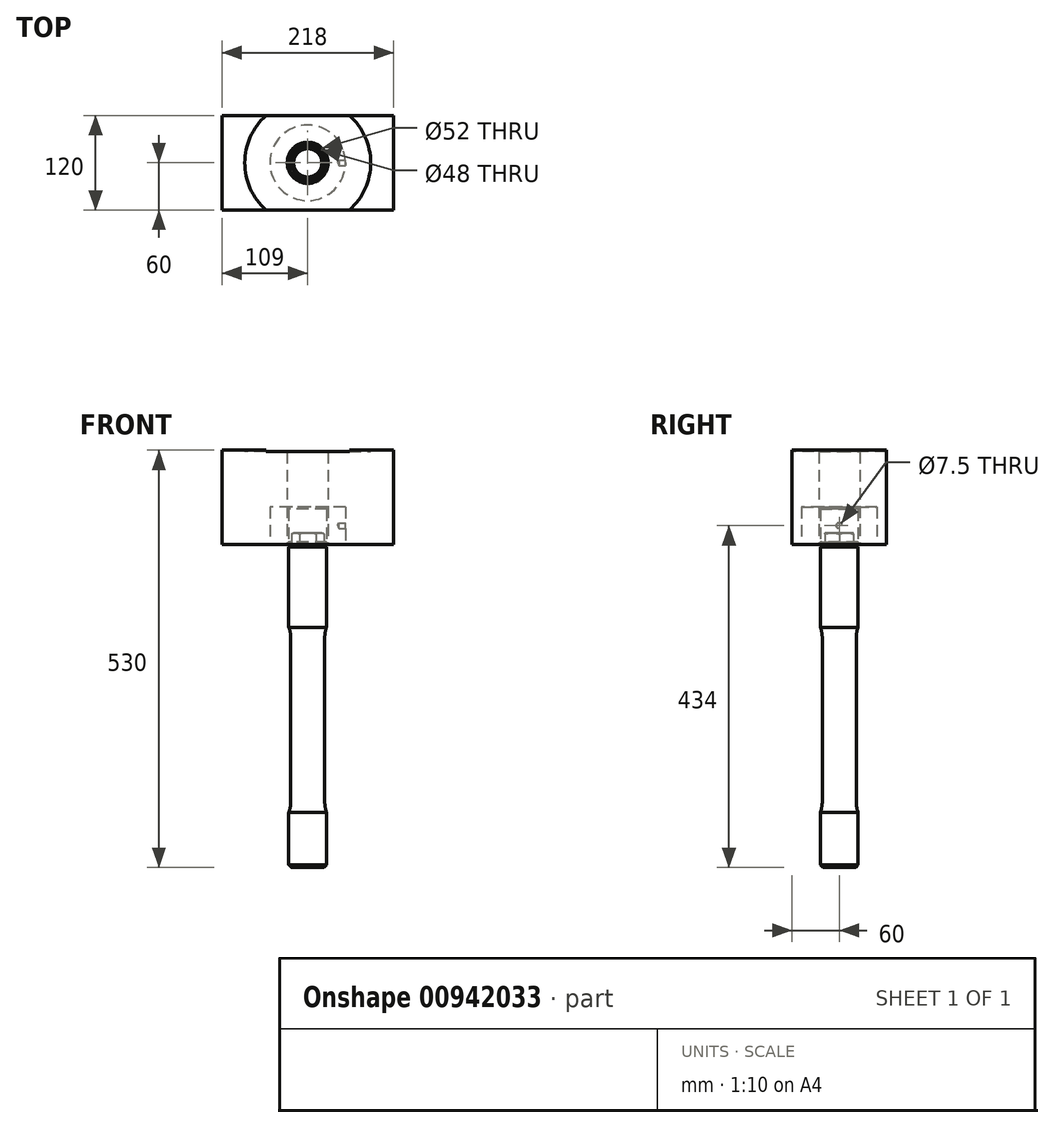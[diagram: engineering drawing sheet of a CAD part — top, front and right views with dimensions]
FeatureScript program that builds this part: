
annotation { "Feature Type Name" : "Feature", "Feature Type Description" : "" }
export const myFeature = defineFeature(function(context is Context, id is Id, definition is map)
    precondition{}
    {
        {
            var Q0;
            Q0=qCreatedBy(makeId("Front.planeOp"),FACE);
            var sketch = newSketch(context, id + "F0", { "sketchPlane" : qUnion([Q0])});
            skLineSegment(sketch, "E0", {"start": v(0, 0) * mm, "end": v(24, 0) * mm});
            skLineSegment(sketch, "E1", {"start": v(24, 0) * mm, "end": v(24, -105) * mm});
            skLineSegment(sketch, "E2", {"start": v(21.65, -117.6) * mm, "end": v(21.65, -327.4) * mm});
            skArc(sketch, "E3", {"start": v(24, -105) * mm, "mid": v(22.24, -111.2) * mm, "end": v(21.65, -117.6) * mm});
            skLineSegment(sketch, "E4", {"start": v(0, 0) * mm, "end": v(0, -410) * mm, "construction": true});
            skArc(sketch, "E5", {"start": v(21.65, -327.4) * mm, "mid": v(22.24, -333.8) * mm, "end": v(24, -340) * mm});
            skLineSegment(sketch, "E6", {"start": v(24, -340) * mm, "end": v(24, -410) * mm});
            skLineSegment(sketch, "E7", {"start": v(24, -410) * mm, "end": v(0, -410) * mm});
            skLineSegment(sketch, "E8", {"start": v(0, 0) * mm, "end": v(0, -410) * mm});
            skSolve(sketch);
        }
        {
            var Q0;
            Q0 = qSketchRegion(id + "F0", true);
            var Q1;
            Q1=sQuery(id+"F0.wireOp",EDGE,"E4");
            revolve(context, id + "F1", {"surfaceOperationType" : NewSurfaceOperationType.NEW, "entities" : qUnion([Q0]), "axis" : qUnion([Q1]), "revolveType" : RevolveType.FULL});
        }
        {
            var Q0;
            Q0=qCreatedBy(makeId("Top.planeOp"),FACE);
            var sketch = newSketch(context, id + "F2", { "sketchPlane" : qUnion([Q0])});
            skCircle(sketch, "E9.cCircle", {"center": v(0, 0) * mm, "radius": 18 * mm, "construction": true});
            skLineSegment(sketch, "E9.0", {"start": v(10.4, -18) * mm, "end": v(-10.4, -18) * mm});
            skLineSegment(sketch, "E9.1", {"start": v(-10.4, -18) * mm, "end": v(-20.78, 0) * mm});
            skLineSegment(sketch, "E9.2", {"start": v(-20.78, 0) * mm, "end": v(-10.4, 18) * mm});
            skLineSegment(sketch, "E9.3", {"start": v(-10.4, 18) * mm, "end": v(10.4, 18) * mm});
            skLineSegment(sketch, "E9.4", {"start": v(10.4, 18) * mm, "end": v(20.78, 0) * mm});
            skLineSegment(sketch, "E9.5", {"start": v(20.78, 0) * mm, "end": v(10.4, -18) * mm});
            skPoint(sketch, "E9.0.midPoint", {"position": v(0, -18) * mm});
            skSolve(sketch);
        }
        {
            var Q0;
            Q0 = qSketchRegion(id + "F2", true);
            extrude(context, id + "F3", {"entities" : qUnion([Q0]), "operationType" : NewBodyOperationType.ADD, "depth" : 15 * mm, "offsetDistance" : 25 * mm});
        }
        {
            var Q0;
            Q0=makeQuery(id+"F1.opRevolve","SWEPT_EDGE",EDGE,{"disambiguationData":[OSD([sQuery(id+"F0.wireOp",EDGE,"E0"),sQuery(id+"F0.wireOp",EDGE,"E1")])]});
            var Q1;
            Q1=makeQuery(id+"F1.opRevolve","SWEPT_EDGE",EDGE,{"disambiguationData":[OSD([sQuery(id+"F0.wireOp",EDGE,"E6"),sQuery(id+"F0.wireOp",EDGE,"E7")])]});
            chamfer(context, id + "F4", {"entities" : qUnion([Q0, Q1]), "width" : 3 * mm, "tangentPropagation" : true});
        }
        {
            var Q0;
            Q0=qCreatedBy(makeId("Front.planeOp"),FACE);
            var sketch = newSketch(context, id + "F5", { "sketchPlane" : qUnion([Q0])});
            skLineSegment(sketch, "E10.0", {"start": v(10.4, 15) * mm, "end": v(-10.4, 15) * mm});
            skLineSegment(sketch, "E11", {"start": v(18, 15) * mm, "end": v(23, 12.11) * mm});
            skLineSegment(sketch, "E12", {"start": v(23, 12.11) * mm, "end": v(23, 15) * mm});
            skLineSegment(sketch, "E13", {"start": v(23, 15) * mm, "end": v(18, 15) * mm});
            skLineSegment(sketch, "E14", {"start": v(0, 0) * mm, "end": v(0, 15) * mm, "construction": true});
            skSolve(sketch);
        }
        {
            var Q0;
            Q0 = qSketchRegion(id + "F5", true);
            var Q1;
            Q1=sQuery(id+"F5.wireOp",EDGE,"E14");
            revolve(context, id + "F6", {"operationType" : NewBodyOperationType.REMOVE, "surfaceOperationType" : NewSurfaceOperationType.NEW, "entities" : qUnion([Q0]), "axis" : qUnion([Q1]), "revolveType" : RevolveType.FULL, "oppositeDirection" : true});
        }
        {
            var Q0;
            Q0=qCreatedBy(makeId("Top.planeOp"),FACE);
            var sketch = newSketch(context, id + "F7", { "sketchPlane" : qUnion([Q0])});
            skCircle(sketch, "E15", {"center": v(0, 0) * mm, "radius": 48 * mm});
            skCircle(sketch, "E16", {"center": v(0, 0) * mm, "radius": 24 * mm});
            skSolve(sketch);
        }
        {
            var Q0;
            Q0 = qSketchRegion(id + "F7", true);
            extrude(context, id + "F8", {"entities" : qUnion([Q0]), "depth" : 48 * mm, "offsetDistance" : 25 * mm});
        }
        {
            var Q0;
            Q0=qCreatedBy(makeId("Front.planeOp"),FACE);
            var sketch = newSketch(context, id + "F9", { "sketchPlane" : qUnion([Q0])});
            skLineSegment(sketch, "E17", {"start": v(48, 48) * mm, "end": v(48, 0) * mm});
            skLineSegment(sketch, "E18", {"start": v(48, 20.25) * mm, "end": v(40, 20.25) * mm});
            skLineSegment(sketch, "E19", {"start": v(40, 20.25) * mm, "end": v(37.83, 24) * mm});
            skLineSegment(sketch, "E20", {"start": v(37.83, 24) * mm, "end": v(48, 24) * mm});
            skLineSegment(sketch, "E21", {"start": v(48, 24) * mm, "end": v(48, 20.25) * mm});
            skLineSegment(sketch, "E22", {"start": v(37.83, 24) * mm, "end": v(48, 24) * mm, "construction": true});
            skLineSegment(sketch, "E23", {"start": v(0, 0) * mm, "end": v(0, 40.82) * mm, "construction": true});
            skSolve(sketch);
        }
        {
            var Q0;
            Q0 = qSketchRegion(id + "F9", true);
            var Q1;
            Q1=sQuery(id+"F9.wireOp",EDGE,"E20");
            revolve(context, id + "F10", {"operationType" : NewBodyOperationType.REMOVE, "surfaceOperationType" : NewSurfaceOperationType.NEW, "entities" : qUnion([Q0]), "axis" : qUnion([Q1]), "revolveType" : RevolveType.FULL, "oppositeDirection" : true});
        }
        {
            var Q0;
            Q0=makeQuery(id+"F8.opExtrude","CAP_EDGE",EDGE,{"disambiguationData":[OSD([sQuery(id+"F7.wireOp",EDGE,"E16")])],"isStart":false});
            var Q1;
            Q1=makeQuery(id+"F8.opExtrude","CAP_EDGE",EDGE,{"disambiguationData":[OSD([sQuery(id+"F7.wireOp",EDGE,"E16")])],"isStart":true});
            chamfer(context, id + "F11", {"entities" : qUnion([Q0, Q1]), "width" : 3 * mm, "tangentPropagation" : true});
        }
        {
            var Q0;
            Q0=qCreatedBy(makeId("Top.planeOp"),FACE);
            var sketch = newSketch(context, id + "F12", { "sketchPlane" : qUnion([Q0])});
            skLineSegment(sketch, "E24.bottom", {"start": v(-109, 60) * mm, "end": v(109, 60) * mm});
            skLineSegment(sketch, "E24.top", {"start": v(-109, -60) * mm, "end": v(109, -60) * mm});
            skLineSegment(sketch, "E24.left", {"start": v(-109, 60) * mm, "end": v(-109, -60) * mm});
            skLineSegment(sketch, "E24.right", {"start": v(109, 60) * mm, "end": v(109, -60) * mm});
            skCircle(sketch, "E25", {"center": v(0, 0) * mm, "radius": 26 * mm});
            skSolve(sketch);
        }
        {
            var Q0;
            Q0 = qSketchRegion(id + "F12", true);
            extrude(context, id + "F13", {"entities" : qUnion([Q0]), "depth" : 120 * mm, "offsetDistance" : 25 * mm});
        }
        {
            var Q0;
            Q0=makeQuery(id+"F13.opExtrude","CAP_FACE",FACE,{"disambiguationData":[OSD([sQuery(id+"F12.wireOp",EDGE,"E24.bottom"),sQuery(id+"F12.wireOp",EDGE,"E24.top"),sQuery(id+"F12.wireOp",EDGE,"E24.left"),sQuery(id+"F12.wireOp",EDGE,"E24.right"),sQuery(id+"F12.wireOp",EDGE,"E25")])],"isStart":false});
            var sketch = newSketch(context, id + "F14", { "sketchPlane" : qUnion([Q0])});
            skCircle(sketch, "E26", {"center": v(0, 0) * mm, "radius": 80 * mm});
            skSolve(sketch);
        }
        {
            var Q0;
            Q0 = qSketchRegion(id + "F14", true);
            extrude(context, id + "F15", {"entities" : qUnion([Q0]), "operationType" : NewBodyOperationType.REMOVE, "oppositeDirection" : true, "depth" : 2 * mm, "offsetDistance" : 25 * mm});
        }
    });
